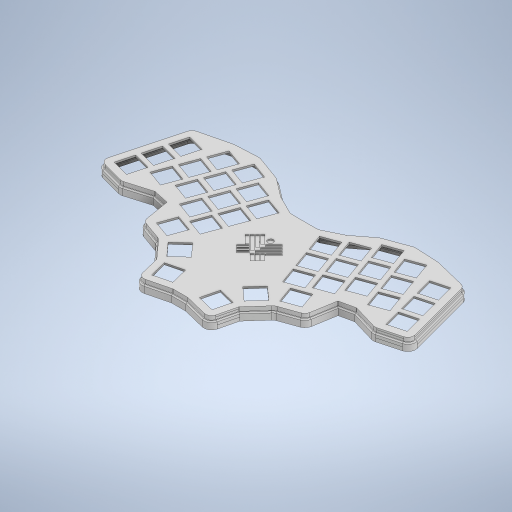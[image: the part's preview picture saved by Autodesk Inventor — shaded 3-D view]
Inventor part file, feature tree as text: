
AUTODESK INVENTOR PART (.ipt)
format: ipt  version: 2024 (Build 280153000, 153)  size: 2,502,656 bytes
history: native  units: mm
features: reference x98, projected_geometry x65, extrude x9, sketch x9, other x5, fillet x3, plane x1, chamfer x1
ambient origin geometry x8: Origin, YZ Plane, XZ Plane, XY Plane, X Axis, Y Axis, Z Axis, Center Point
bodies: Body1 (feature_tree)
feature tree (191):
  extrude  "Extrusion2"  Depth=9.25mm TaperAngle=0.0deg
  sketch  "Skizze5"  dims[d6=0.5mm d7=0.0mm d8=3.5mm d9=0.0mm]
  plane  "Arbeitsebene1"
  extrude  "Extrusion3"  Depth=3.5mm TaperAngle=0.0deg
  extrude  "Extrusion4"  Depth=2.0mm TaperAngle=0.0deg
  extrude  "Extrusion5"  Depth=2.9mm
  extrude  "Extrusion6"  Depth=2.0mm
  extrude  "Extrusion7"  Depth=10.0mm
  fillet  "Rundung1"  Radius=1.5mm
  fillet  "Rundung2"  Radius=10.0mm
  fillet  "Rundung3"  Radius=10.0mm
  extrude  "Extrusion8"  Depth=0.9mm TaperAngle=45.0deg
  extrude  "Extrusion9"  [1 undecoded]
  extrude  "Extrusion10"  [1 undecoded]
  chamfer  "Fasen1"  [1 undecoded]
  sketch  "Skizze3"  dims[d2=1.5mm d3=0.0mm d4=9.25mm d5=0.0mm]
  reference  "Referenz84"
  reference  "Referenz85"
  reference  "Referenz86"
  reference  "Referenz87"
  reference  "Referenz88"
  reference  "Referenz89"
  reference  "Referenz90"
  reference  "Referenz91"
  reference  "Referenz92"
  reference  "Referenz93"
  reference  "Referenz94"
  reference  "Referenz95"
  reference  "Referenz96"
  reference  "Referenz97"
  reference  "Referenz98"
  reference  "Referenz99"
  reference  "Referenz100"
  reference  "Referenz101"
  reference  "Referenz102"
  reference  "Referenz103"
  reference  "Referenz104"
  reference  "Referenz105"
  reference  "Referenz106"
  reference  "Referenz107"
  reference  "Referenz108"
  reference  "Referenz109"
  reference  "Referenz110"
  reference  "Referenz111"
  reference  "Referenz112"
  reference  "Referenz113"
  reference  "Referenz114"
  reference  "Referenz115"
  reference  "Referenz116"
  reference  "Referenz117"
  reference  "Referenz118"
  reference  "Referenz119"
  reference  "Referenz120"
  reference  "Referenz121"
  reference  "Referenz122"
  reference  "Referenz123"
  reference  "Referenz124"
  reference  "Referenz125"
  reference  "Referenz126"
  reference  "Referenz127"
  projected_geometry  "Projizierte Kontur56"
  reference  "Referenz133"
  reference  "Referenz134"
  reference  "Referenz135"
  reference  "Referenz136"
  reference  "Referenz137"
  reference  "Referenz138"
  reference  "Referenz139"
  reference  "Referenz140"
  reference  "Referenz141"
  reference  "Referenz142"
  reference  "Referenz143"
  reference  "Referenz144"
  reference  "Referenz145"
  reference  "Referenz146"
  reference  "Referenz147"
  reference  "Referenz148"
  reference  "Referenz149"
  reference  "Referenz150"
  reference  "Referenz151"
  reference  "Referenz152"
  reference  "Referenz153"
  reference  "Referenz154"
  reference  "Referenz155"
  reference  "Referenz156"
  reference  "Referenz157"
  reference  "Referenz158"
  reference  "Referenz159"
  reference  "Referenz160"
  reference  "Referenz161"
  reference  "Referenz162"
  reference  "Referenz163"
  sketch  "Skizze6"  dims[d10=1.0mm d11=2.0mm d12=0.0mm]
  projected_geometry  "Projizierte Kontur57"
  sketch  "Skizze7"  dims[d13=2.9mm d14=2.9mm]
  reference  "Referenz164"
  reference  "Referenz165"
  reference  "Referenz166"
  reference  "Referenz167"
  reference  "Referenz168"
  reference  "Referenz169"
  reference  "Referenz170"
  reference  "Referenz171"
  reference  "Referenz172"
  reference  "Referenz173"
  reference  "Referenz174"
  reference  "Referenz175"
  reference  "Referenz176"
  reference  "Referenz177"
  reference  "Referenz178"
  reference  "Referenz179"
  reference  "Referenz180"
  reference  "Referenz181"
  reference  "Referenz182"
  reference  "Referenz183"
  reference  "Referenz184"
  reference  "Referenz185"
  reference  "Referenz186"
  sketch  "Skizze9"  dims[d15=3.0mm d16=0.0mm d17=2.0mm]
  projected_geometry  "Projizierte Kontur58"
  sketch  "Skizze10"  dims[d18=2.0mm d19=0.75mm d20=1.5mm d21=10.0mm d22=0.0mm d23=10.0mm d24=0.0mm]
  sketch  "Skizze11"  dims[d25=3.25mm d26=0.0mm d27=0.9mm d28=2.0mm d29=45.0deg]
  projected_geometry  "Projizierte Kontur61"
  sketch  "Skizze13"
  projected_geometry  "Projizierte Kontur62"
  projected_geometry  "Projizierte Kontur63"
  projected_geometry  "Projizierte Kontur64"
  projected_geometry  "Projizierte Kontur65"
  projected_geometry  "Projizierte Kontur66"
  projected_geometry  "Projizierte Kontur67"
  projected_geometry  "Projizierte Kontur68"
  projected_geometry  "Projizierte Kontur69"
  projected_geometry  "Projizierte Kontur70"
  projected_geometry  "Projizierte Kontur71"
  projected_geometry  "Projizierte Kontur72"
  projected_geometry  "Projizierte Kontur73"
  projected_geometry  "Projizierte Kontur74"
  projected_geometry  "Projizierte Kontur75"
  projected_geometry  "Projizierte Kontur76"
  projected_geometry  "Projizierte Kontur77"
  projected_geometry  "Projizierte Kontur78"
  projected_geometry  "Projizierte Kontur79"
  projected_geometry  "Projizierte Kontur80"
  projected_geometry  "Projizierte Kontur81"
  projected_geometry  "Projizierte Kontur82"
  projected_geometry  "Projizierte Kontur83"
  projected_geometry  "Projizierte Kontur84"
  projected_geometry  "Projizierte Kontur85"
  projected_geometry  "Projizierte Kontur86"
  projected_geometry  "Projizierte Kontur87"
  projected_geometry  "Projizierte Kontur88"
  projected_geometry  "Projizierte Kontur89"
  projected_geometry  "Projizierte Kontur90"
  projected_geometry  "Projizierte Kontur91"
  projected_geometry  "Projizierte Kontur92"
  projected_geometry  "Projizierte Kontur93"
  projected_geometry  "Projizierte Kontur94"
  projected_geometry  "Projizierte Kontur95"
  projected_geometry  "Projizierte Kontur96"
  projected_geometry  "Projizierte Kontur97"
  projected_geometry  "Projizierte Kontur98"
  projected_geometry  "Projizierte Kontur99"
  projected_geometry  "Projizierte Kontur100"
  projected_geometry  "Projizierte Kontur101"
  projected_geometry  "Projizierte Kontur102"
  projected_geometry  "Projizierte Kontur103"
  projected_geometry  "Projizierte Kontur104"
  projected_geometry  "Projizierte Kontur105"
  projected_geometry  "Projizierte Kontur106"
  projected_geometry  "Projizierte Kontur107"
  projected_geometry  "Projizierte Kontur108"
  projected_geometry  "Projizierte Kontur109"
  projected_geometry  "Projizierte Kontur110"
  projected_geometry  "Projizierte Kontur111"
  projected_geometry  "Projizierte Kontur112"
  projected_geometry  "Projizierte Kontur113"
  projected_geometry  "Projizierte Kontur114"
  projected_geometry  "Projizierte Kontur115"
  projected_geometry  "Projizierte Kontur116"
  projected_geometry  "Projizierte Kontur117"
  projected_geometry  "Projizierte Kontur118"
  projected_geometry  "Projizierte Kontur119"
  projected_geometry  "Projizierte Kontur120"
  projected_geometry  "Projizierte Kontur121"
  sketch  "Skizze14"
  projected_geometry  "Projizierte Kontur122"
  other  "<userpath>\OneDrive\Keyboards\Blavinge\case\1-part\top.iam"
  other  "top.iam"
  other  "middle_top:1"
  other  "left_top:1"
  other  "left_top_MIR:1"
note: 3 required parameter values undecoded (feature->parameter linkage not recoverable at this tier; creation-order binding heuristic only, values carry confidence <= 0.55)
